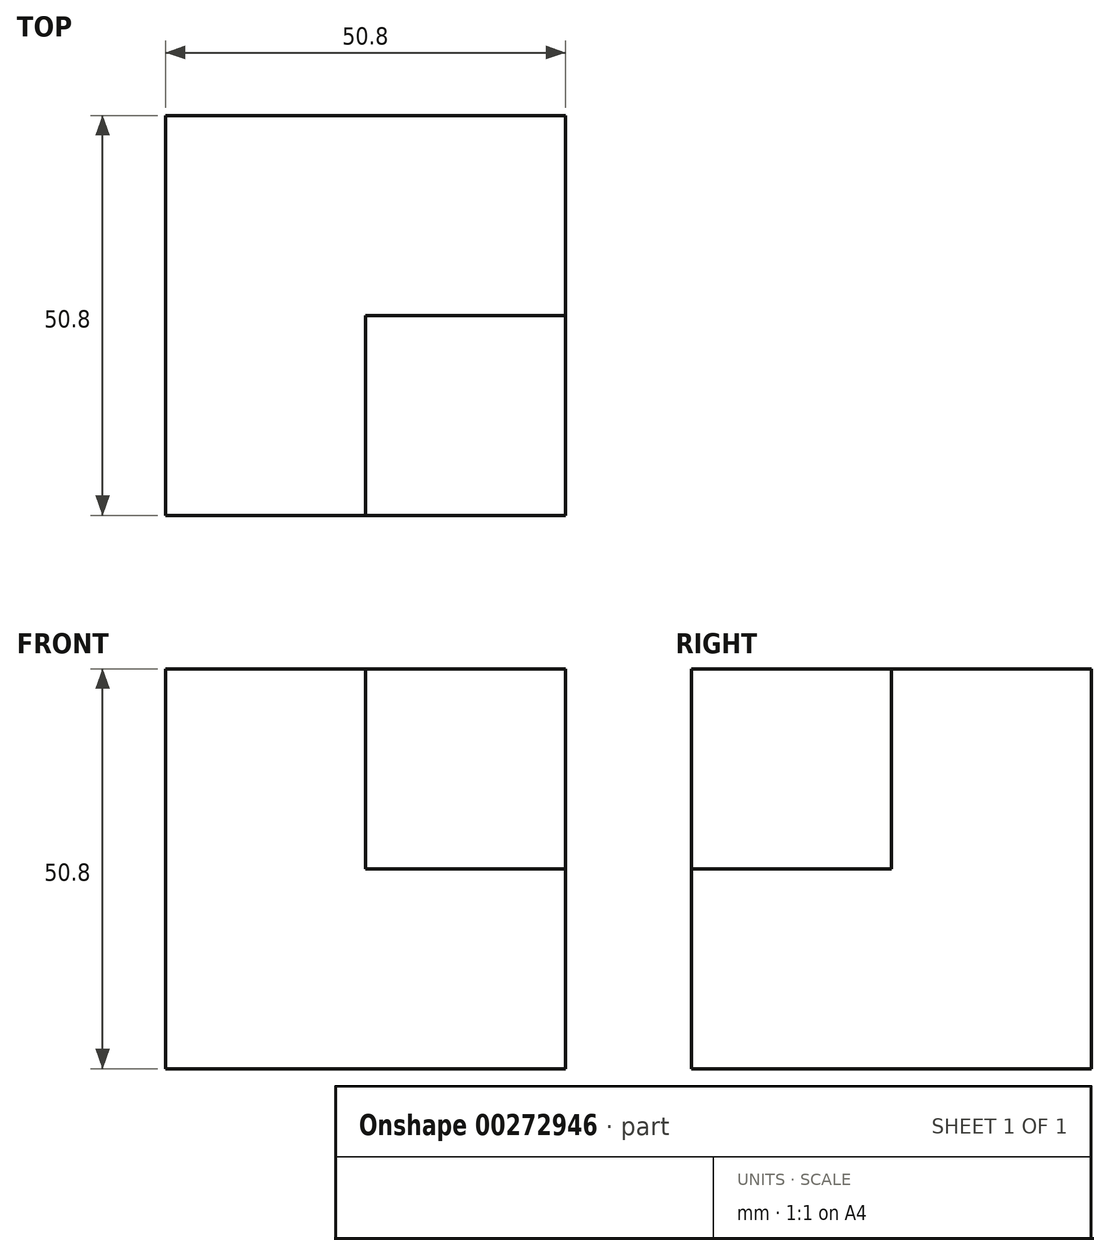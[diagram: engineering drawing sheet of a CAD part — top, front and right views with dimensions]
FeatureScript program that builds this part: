
annotation { "Feature Type Name" : "Feature", "Feature Type Description" : "" }
export const myFeature = defineFeature(function(context is Context, id is Id, definition is map)
    precondition{}
    {
        {
            var Q0;
            Q0=qCreatedBy(makeId("Front.planeOp"),FACE);
            var sketch = newSketch(context, id + "F0", { "sketchPlane" : qUnion([Q0])});
            skLineSegment(sketch, "E0.bottom", {"start": v(-1.71, 0) * mm, "end": v(-52.51, 0) * mm});
            skLineSegment(sketch, "E0.top", {"start": v(-1.71, 50.8) * mm, "end": v(-52.51, 50.8) * mm});
            skLineSegment(sketch, "E0.left", {"start": v(-1.71, 0) * mm, "end": v(-1.71, 50.8) * mm});
            skLineSegment(sketch, "E0.right", {"start": v(-52.51, 0) * mm, "end": v(-52.51, 50.8) * mm});
            skSolve(sketch);
        }
        {
            var Q0;
            Q0=makeQuery(id+"F0.imprint","IMPRINT",FACE,{"disambiguationData":[TD([[makeQuery(id+"F0.imprint","IMPRINT",EDGE,{"derivedFrom":sQuery(id+"F0.wireOp",EDGE,"E0.bottom")}),-1.0]])]});
            extrude(context, id + "F1", {"entities" : qUnion([Q0]), "depth" : 50.8 * mm});
        }
        {
            var Q0;
            Q0=makeQuery(id+"F1.opExtrude","CAP_FACE",FACE,{"disambiguationData":[OSD([sQuery(id+"F0.wireOp",EDGE,"E0.bottom"),sQuery(id+"F0.wireOp",EDGE,"E0.top"),sQuery(id+"F0.wireOp",EDGE,"E0.left"),sQuery(id+"F0.wireOp",EDGE,"E0.right")])],"isStart":false});
            var sketch = newSketch(context, id + "F2", { "sketchPlane" : qUnion([Q0])});
            skLineSegment(sketch, "E1.bottom", {"start": v(-52.51, 50.8) * mm, "end": v(-27.11, 50.8) * mm});
            skLineSegment(sketch, "E1.top", {"start": v(-52.51, 25.4) * mm, "end": v(-27.11, 25.4) * mm});
            skLineSegment(sketch, "E1.left", {"start": v(-52.51, 50.8) * mm, "end": v(-52.51, 25.4) * mm});
            skLineSegment(sketch, "E1.right", {"start": v(-27.11, 50.8) * mm, "end": v(-27.11, 25.4) * mm});
            skSolve(sketch);
        }
        {
            var Q0;
            Q0 = qSketchRegion(id + "F2", true);
            extrude(context, id + "F3", {"entities" : qUnion([Q0]), "operationType" : NewBodyOperationType.REMOVE, "depth" : 50.8 * mm});
        }
        {
            var Q0;
            Q0=makeQuery(id+"F1.opExtrude","CAP_FACE",FACE,{"disambiguationData":[OSD([sQuery(id+"F0.wireOp",EDGE,"E0.bottom"),sQuery(id+"F0.wireOp",EDGE,"E0.top"),sQuery(id+"F0.wireOp",EDGE,"E0.left"),sQuery(id+"F0.wireOp",EDGE,"E0.right")])],"isStart":false});
            var sketch = newSketch(context, id + "F4", { "sketchPlane" : qUnion([Q0])});
            skLineSegment(sketch, "E2.bottom", {"start": v(-27.11, 50.8) * mm, "end": v(-1.71, 50.8) * mm});
            skLineSegment(sketch, "E2.top", {"start": v(-27.11, 25.4) * mm, "end": v(-1.71, 25.4) * mm});
            skLineSegment(sketch, "E2.left", {"start": v(-27.11, 50.8) * mm, "end": v(-27.11, 25.4) * mm});
            skLineSegment(sketch, "E2.right", {"start": v(-1.71, 50.8) * mm, "end": v(-1.71, 25.4) * mm});
            skSolve(sketch);
        }
        {
            var Q0;
            Q0=makeQuery(id+"F4.imprint","IMPRINT",FACE,{"disambiguationData":[TD([[makeQuery(id+"F4.imprint","IMPRINT",EDGE,{"derivedFrom":sQuery(id+"F4.wireOp",EDGE,"E2.bottom")}),1.0]])]});
            extrude(context, id + "F5", {"entities" : qUnion([Q0]), "operationType" : NewBodyOperationType.REMOVE, "oppositeDirection" : true, "depth" : 25.4 * mm});
        }
    });
